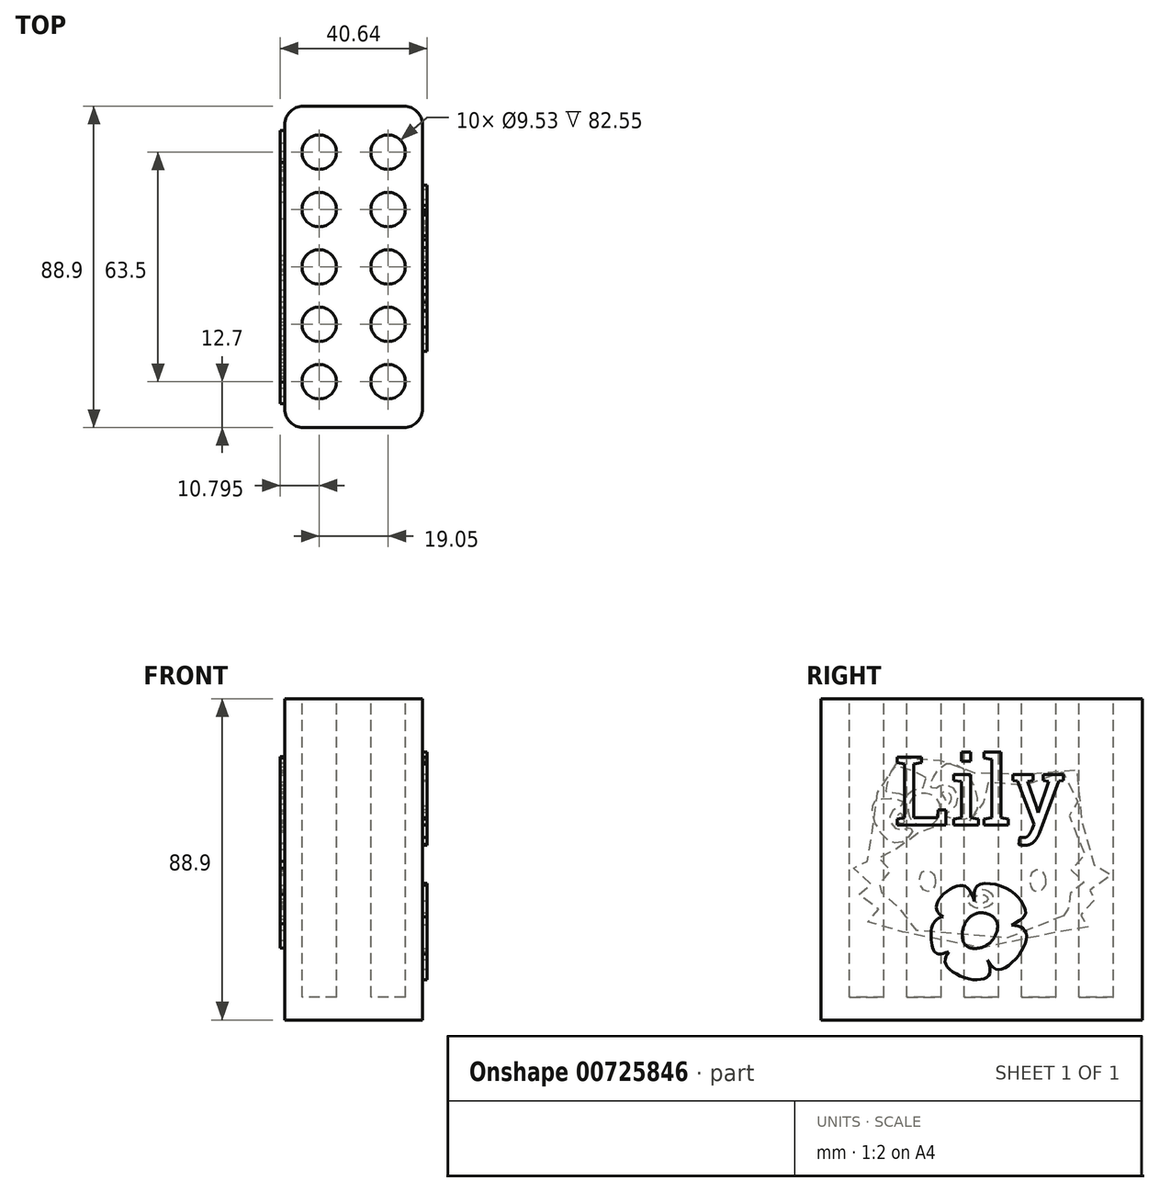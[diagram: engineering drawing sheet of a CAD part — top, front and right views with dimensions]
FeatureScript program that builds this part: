
annotation { "Feature Type Name" : "Feature", "Feature Type Description" : "" }
export const myFeature = defineFeature(function(context is Context, id is Id, definition is map)
    precondition{}
    {
        {
            var Q0;
            Q0=qCreatedBy(makeId("Right.planeOp"),FACE);
            var sketch = newSketch(context, id + "F0", { "sketchPlane" : qUnion([Q0])});
            skLineSegment(sketch, "E0.bottom", {"start": v(-44.45, 44.45) * mm, "end": v(44.45, 44.45) * mm});
            skLineSegment(sketch, "E0.top", {"start": v(-44.45, -44.45) * mm, "end": v(44.45, -44.45) * mm});
            skLineSegment(sketch, "E0.left", {"start": v(-44.45, 44.45) * mm, "end": v(-44.45, -44.45) * mm});
            skLineSegment(sketch, "E0.right", {"start": v(44.45, 44.45) * mm, "end": v(44.45, -44.45) * mm});
            skPoint(sketch, "E0.middle", {"position": v(0, 0) * mm});
            skSolve(sketch);
        }
        {
            var Q0;
            Q0=qSketchRegion(id+"F0",true);
            extrude(context, id + "F1", {"entities" : qUnion([Q0]), "endBound" : BoundingType.SYMMETRIC, "depth" : 38.1 * mm, "offsetDistance" : 25.4 * mm});
        }
        {
            var Q0;
            Q0=makeQuery(id+"F1.opExtrude","SWEPT_FACE",FACE,{"disambiguationData":[OSD([sQuery(id+"F0.wireOp",EDGE,"E0.bottom")])]});
            var sketch = newSketch(context, id + "F2", { "sketchPlane" : qUnion([Q0])});
            skCircle(sketch, "E1", {"center": v(-9.52, -31.75) * mm, "radius": 4.76 * mm});
            skCircle(sketch, "E2", {"center": v(-9.52, 0) * mm, "radius": 4.76 * mm});
            skCircle(sketch, "E3", {"center": v(-9.52, -15.88) * mm, "radius": 4.76 * mm});
            skCircle(sketch, "E4", {"center": v(-9.52, 15.88) * mm, "radius": 4.76 * mm});
            skCircle(sketch, "E5", {"center": v(-9.52, 31.75) * mm, "radius": 4.76 * mm});
            skCircle(sketch, "E6.MirrorC", {"center": v(9.52, 0) * mm, "radius": 4.76 * mm});
            skCircle(sketch, "E7.MirrorC", {"center": v(9.52, -31.75) * mm, "radius": 4.76 * mm});
            skCircle(sketch, "E8.MirrorC", {"center": v(9.52, -15.88) * mm, "radius": 4.76 * mm});
            skCircle(sketch, "E9.MirrorC", {"center": v(9.52, 15.88) * mm, "radius": 4.76 * mm});
            skCircle(sketch, "E10.MirrorC", {"center": v(9.52, 31.75) * mm, "radius": 4.76 * mm});
            skSolve(sketch);
        }
        {
            var Q0;
            Q0=qSketchRegion(id+"F2",true);
            extrude(context, id + "F3", {"entities" : qUnion([Q0]), "operationType" : NewBodyOperationType.REMOVE, "oppositeDirection" : true, "depth" : 82.55 * mm, "offsetDistance" : 25.4 * mm});
        }
        {
            var Q0;
            Q0=makeQuery(id+"F1.opExtrude","CAP_FACE",FACE,{"disambiguationData":[OSD([sQuery(id+"F0.wireOp",EDGE,"E0.bottom"),sQuery(id+"F0.wireOp",EDGE,"E0.top"),sQuery(id+"F0.wireOp",EDGE,"E0.left"),sQuery(id+"F0.wireOp",EDGE,"E0.right")])],"isStart":false});
            var sketch = newSketch(context, id + "F4", { "sketchPlane" : qUnion([Q0])});
            skText(sketch, "E11", { "text": "Lily", "fontName": "RobotoSlab-Regular.ttf"});
            const initialGuessF4  = {"E11": [-0.0243, 0.00952, 1, 0, 0.01905]};
            skSetInitialGuess(sketch, initialGuessF4);
            skSolve(sketch);
        }
        {
            var Q0;
            Q0=qSketchRegion(id+"F4",true);
            extrude(context, id + "F5", {"entities" : qUnion([Q0]), "operationType" : NewBodyOperationType.ADD, "depth" : 1.27 * mm, "offsetDistance" : 25.4 * mm});
        }
        {
            var Q0;
            Q0=makeQuery(id+"F1.opExtrude","CAP_EDGE",EDGE,{"disambiguationData":[OSD([sQuery(id+"F0.wireOp",EDGE,"E0.left")])],"isStart":false});
            var Q1;
            Q1=makeQuery(id+"F1.opExtrude","CAP_EDGE",EDGE,{"disambiguationData":[OSD([sQuery(id+"F0.wireOp",EDGE,"E0.right")])],"isStart":false});
            var Q2;
            Q2=makeQuery(id+"F1.opExtrude","CAP_EDGE",EDGE,{"disambiguationData":[OSD([sQuery(id+"F0.wireOp",EDGE,"E0.right")])],"isStart":true});
            var Q3;
            Q3=makeQuery(id+"F1.opExtrude","CAP_EDGE",EDGE,{"disambiguationData":[OSD([sQuery(id+"F0.wireOp",EDGE,"E0.left")])],"isStart":true});
            fillet(context, id + "F6", {"entities" : qUnion([Q0, Q1, Q2, Q3]), "radius" : 5.08 * mm, "tangentPropagation" : true, "allowEdgeOverflow" : false});
        }
        {
            var Q0;
            {var subQ0=sQuery(id+"F0.wireOp",EDGE,"E0.right");var subQ1=sQuery(id+"F0.wireOp",EDGE,"E0.left");var subQ2=sQuery(id+"F0.wireOp",EDGE,"E0.top");var subQ3=sQuery(id+"F0.wireOp",EDGE,"E0.bottom");Q0=makeQuery(id+"F5.boolean.opBoolean","SPLIT",FACE,{"disambiguationData":[TD([makeQuery(id+"F1.opExtrude","SWEPT_FACE",FACE,{"disambiguationData":[OSD([subQ3])]})])],"derivedFrom":makeQuery(id+"F1.opExtrude","CAP_FACE",FACE,{"disambiguationData":[OSD([subQ3,subQ2,subQ1,subQ0])],"isStart":false})});}
            var sketch = newSketch(context, id + "F7", { "sketchPlane" : qUnion([Q0])});
            skFitSpline(sketch, "E12", {"points": [v(-4.86, -18.4) * mm, v(-4.86, -23.15) * mm, v(-2.54, -24.6) * mm, v(1.63, -23.63) * mm, v(4.35, -19.56) * mm, v(3.48, -16.16) * mm, v(-1.08, -14.9) * mm, v(-4.86, -18.4) * mm]});
            skFitSpline(sketch, "E13", {"points": [v(-1.08, -14.9) * mm, v(-2.63, -9.86) * mm, v(-5.16, -7.24) * mm, v(-10.68, -9.86) * mm, v(-12.53, -13.64) * mm, v(-10.68, -15.97) * mm], "startDerivative": vector(-5.93, 23.88) * mm, "endDerivative": vector(15.22, -12.78) * mm});
            skFitSpline(sketch, "E14", {"points": [v(-4.47, -17.57) * mm, v(-10.68, -15.97) * mm, v(-13.6, -18.4) * mm, v(-13.5, -24.5) * mm, v(-11.85, -26.25) * mm, v(-4.86, -23.15) * mm], "startDerivative": vector(-29.8, 12.2) * mm, "endDerivative": vector(33.44, 19.83) * mm});
            skFitSpline(sketch, "E15", {"points": [v(-9.16, -25.52) * mm, v(-9.89, -29.04) * mm, v(-2.87, -33.2) * mm, v(2.18, -31.73) * mm, v(0, -24.4) * mm], "startDerivative": vector(-9.58, -18.07) * mm, "endDerivative": vector(-15.48, 30.39) * mm});
            skFitSpline(sketch, "E16", {"points": [v(1.63, -27.8) * mm, v(4.55, -30.51) * mm, v(10.58, -26.1) * mm, v(12.21, -20.07) * mm, v(9.2, -18.28) * mm, v(4.44, -18.85) * mm], "startDerivative": vector(13.9, -22.16) * mm, "endDerivative": vector(-25, -5.78) * mm});
            skFitSpline(sketch, "E17", {"points": [v(-2, -11.56) * mm, v(-1, -7.27) * mm, v(6.67, -7.92) * mm, v(11.4, -12.32) * mm, v(12.05, -15.34) * mm, v(8.3, -18.23) * mm], "startDerivative": vector(-1.04, 28.17) * mm, "endDerivative": vector(-25.73, -13.95) * mm});
            skSolve(sketch);
        }
        {
            var Q0;
            Q0=qSketchRegion(id+"F7",true);
            extrude(context, id + "F8", {"entities" : qUnion([Q0]), "operationType" : NewBodyOperationType.ADD, "depth" : 1.27 * mm, "offsetDistance" : 25.4 * mm});
        }
        {
            var Q0;
            Q0=makeQuery(id+"F1.opExtrude","CAP_FACE",FACE,{"disambiguationData":[OSD([sQuery(id+"F0.wireOp",EDGE,"E0.bottom"),sQuery(id+"F0.wireOp",EDGE,"E0.top"),sQuery(id+"F0.wireOp",EDGE,"E0.left"),sQuery(id+"F0.wireOp",EDGE,"E0.right")])],"isStart":true});
            var sketch = newSketch(context, id + "F9", { "sketchPlane" : qUnion([Q0])});
            skFitSpline(sketch, "E18", {"points": [v(-22.7, -15.64) * mm, v(-20.05, -17.5) * mm, v(-15, -19.89) * mm, v(-7.32, -21.74) * mm, v(3.38, -22.27) * mm, v(17.67, -19.77) * mm, v(21.35, -17.76) * mm, v(24, -15.35) * mm, v(24.27, -15) * mm, v(24.16, -14.66) * mm, v(23.37, -14.2) * mm, v(22.87, -13.33) * mm, v(23.28, -12.82) * mm, v(24.47, -12.89) * mm, v(25.28, -13.05) * mm, v(25.7, -12.94) * mm, v(26.37, -12.04) * mm, v(27.2, -10.17) * mm, v(27.48, -9.4) * mm, v(27.45, -9.11) * mm, v(27.27, -8.9) * mm, v(26.5, -8.65) * mm, v(25.8, -8.32) * mm, v(25.56, -7.73) * mm, v(25.82, -7.37) * mm, v(26.64, -7.16) * mm, v(27.64, -7.18) * mm, v(28.07, -7) * mm, v(28.36, -5.76) * mm, v(28.55, -3.62) * mm, v(28.53, -3.02) * mm, v(28.35, -2.83) * mm, v(28, -2.8) * mm, v(26.67, -2.99) * mm, v(25.65, -3.11) * mm, v(25.12, -3.14) * mm, v(24.61, -2.83) * mm, v(24.47, -2.63) * mm, v(24.51, -2.04) * mm, v(25.33, -1.48) * mm, v(26.78, -1.18) * mm, v(28.2, -0.93) * mm, v(28.46, -0.61) * mm, v(28.46, 0.39) * mm, v(28.22, 1.8) * mm, v(27.98, 2.96) * mm, v(27.52, 4.34) * mm, v(27.47, 4.39) * mm, v(27.18, 4.14) * mm, v(25.74, 3.3) * mm, v(23.42, 2.8) * mm, v(21.84, 3.07) * mm, v(20.58, 3.69) * mm, v(19.46, 4.52) * mm, v(18.5, 5.68) * mm, v(17.9, 6.57) * mm, v(17.6, 7.23) * mm, v(17.5, 7.7) * mm, v(17.4, 7.8) * mm, v(17.14, 7.72) * mm, v(15.94, 7.6) * mm, v(14.07, 7.89) * mm, v(12.84, 8.36) * mm, v(11.63, 9.25) * mm, v(10.84, 10.06) * mm, v(10.7, 10.28) * mm, v(10.6, 10.37) * mm, v(10.5, 10.3) * mm, v(10.1, 10.05) * mm, v(8.73, 9.63) * mm, v(7.2, 9.31) * mm, v(5.52, 9.16) * mm, v(3.95, 9.32) * mm, v(2.59, 9.8) * mm, v(1.24, 10.63) * mm, v(0.42, 11.8) * mm, v(0, 12.53) * mm, v(-0.49, 13.98) * mm, v(-0.58, 16.42) * mm, v(-0.26, 18.09) * mm, v(0.3, 20.32) * mm, v(0.55, 21.1) * mm, v(0.68, 21.34) * mm, v(0.58, 21.39) * mm, v(-0.33, 21.39) * mm, v(-3.85, 21.29) * mm, v(-6.48, 21.17) * mm, v(-9.03, 21.01) * mm, v(-10.65, 20.59) * mm, v(-11.67, 20.46) * mm, v(-12.7, 20.71) * mm, v(-14.98, 21.85) * mm, v(-16.95, 22.8) * mm, v(-19.76, 23.7) * mm, v(-22.15, 24.23) * mm, v(-23.69, 23.95) * mm, v(-24.9, 22.89) * mm, v(-25.83, 21.12) * mm, v(-26.45, 18.6) * mm, v(-26.58, 16.45) * mm, v(-26.37, 14.7) * mm, v(-26.03, 13.8) * mm, v(-25.87, 13.42) * mm, v(-25.73, 13.32) * mm, v(-25.35, 13.47) * mm, v(-24.67, 13.72) * mm, v(-24.13, 13.51) * mm, v(-23.91, 12.78) * mm, v(-24.38, 11.75) * mm, v(-26.02, 9.33) * mm, v(-27.42, 6.06) * mm, v(-28.21, 3.37) * mm, v(-28.6, 1.53) * mm, v(-28.84, -0.28) * mm, v(-28.87, -1.3) * mm, v(-28.8, -1.87) * mm, v(-28.48, -2.1) * mm, v(-27.35, -2.22) * mm, v(-26, -2.55) * mm, v(-25.1, -2.78) * mm, v(-24.65, -3.33) * mm, v(-24.96, -3.98) * mm, v(-26, -4.12) * mm, v(-27.34, -4.08) * mm, v(-28.23, -4.08) * mm, v(-28.5, -4.28) * mm, v(-28.53, -5) * mm, v(-28.28, -6.53) * mm, v(-27.84, -7.8) * mm, v(-27.59, -8.48) * mm, v(-27.3, -8.5) * mm, v(-26.7, -8.5) * mm, v(-25.5, -8.4) * mm, v(-24.6, -8.55) * mm, v(-24.21, -8.98) * mm, v(-24.57, -9.44) * mm, v(-25.95, -10.1) * mm, v(-26.7, -10.33) * mm, v(-26.53, -11.02) * mm, v(-25.9, -12.12) * mm, v(-25.13, -13.1) * mm, v(-24.77, -13.64) * mm, v(-24.24, -13.81) * mm, v(-23.3, -13.62) * mm, v(-21.96, -13.17) * mm, v(-21.2, -13.17) * mm, v(-20.82, -13.81) * mm, v(-21.04, -14.36) * mm, v(-22.26, -15.1) * mm, v(-22.64, -15.31) * mm, v(-22.73, -15.48) * mm, v(-22.7, -15.64) * mm]});
            skFitSpline(sketch, "E19", {"points": [v(-29.43, -18.69) * mm, v(-27.61, -17.61) * mm, v(-25.93, -16.85) * mm, v(-25.35, -16.61) * mm, v(-24.51, -17.08) * mm, v(-21.83, -19.06) * mm, v(-17.07, -21.47) * mm, v(-11.95, -23.29) * mm, v(-4.4, -24.23) * mm, v(2.24, -24.57) * mm, v(9.78, -24) * mm, v(19.8, -21.24) * mm, v(24.82, -17.78) * mm, v(26.43, -16.28) * mm, v(26.77, -15.9) * mm, v(27.23, -15.72) * mm, v(28.23, -16.02) * mm, v(30.56, -16.94) * mm, v(32.3, -17.67) * mm, v(32.87, -17.83) * mm, v(33.45, -17.38) * mm, v(33.34, -16.58) * mm, v(32.06, -15.5) * mm, v(30.15, -14.58) * mm, v(28.67, -13.95) * mm, v(28.38, -13.7) * mm, v(28.37, -13.17) * mm, v(29.21, -11.25) * mm, v(29.77, -9.94) * mm, v(30.04, -9.44) * mm, v(30.7, -9.34) * mm, v(32.26, -9.47) * mm, v(33.73, -9.7) * mm, v(35.38, -9.58) * mm, v(35.82, -9.19) * mm, v(35.4, -8.52) * mm, v(33.65, -7.86) * mm, v(31.73, -7.55) * mm, v(30.98, -7.45) * mm, v(30.65, -7.26) * mm, v(30.54, -6.95) * mm, v(30.64, -5.4) * mm, v(30.85, -3.4) * mm, v(30.85, -2.86) * mm, v(30.99, -2.63) * mm, v(31.36, -2.48) * mm, v(32.86, -2.35) * mm, v(34.6, -2.4) * mm, v(35.94, -2.42) * mm, v(36.96, -2.4) * mm, v(37.55, -2.21) * mm, v(37.8, -1.77) * mm, v(37.41, -1.23) * mm, v(35.83, -0.78) * mm, v(33.04, -0.57) * mm, v(31.39, -0.56) * mm, v(31.06, -0.48) * mm, v(30.75, 0.23) * mm, v(30.23, 3.59) * mm, v(29.5, 5.69) * mm, v(29.27, 6.34) * mm, v(29.28, 6.4) * mm, v(29.55, 6.79) * mm, v(30.72, 8.9) * mm, v(31.71, 11.95) * mm, v(31.65, 15.49) * mm, v(30.32, 17.65) * mm, v(28.79, 18.2) * mm, v(28.75, 18.27) * mm, v(28.7, 19) * mm, v(27.96, 23.26) * mm, v(26.76, 26.2) * mm, v(25.02, 27.79) * mm, v(23.03, 28.03) * mm, v(20.07, 27.57) * mm, v(15.98, 25.93) * mm, v(14.3, 24.8) * mm, v(14.18, 24.71) * mm, v(14.1, 24.76) * mm, v(11.96, 27.01) * mm, v(9.57, 28.26) * mm, v(6.5, 28.03) * mm, v(4.35, 26.75) * mm, v(2.93, 25.1) * mm, v(2.15, 24.03) * mm, v(2.06, 24) * mm, v(-0.2, 24.06) * mm, v(-5.9, 23.96) * mm, v(-10.05, 23.43) * mm, v(-11.32, 23.27) * mm, v(-13.79, 24.17) * mm, v(-19.2, 26.17) * mm, v(-22.67, 26.7) * mm, v(-25.3, 26) * mm, v(-26.87, 23.7) * mm, v(-28.56, 18.86) * mm, v(-28.71, 14.18) * mm, v(-27.71, 11.13) * mm, v(-27.75, 10.52) * mm, v(-28.2, 9.65) * mm, v(-29.48, 6.76) * mm, v(-30.81, 2.79) * mm, v(-31.1, 0) * mm, v(-31.19, -1.43) * mm, v(-31.29, -1.9) * mm, v(-31.9, -2.06) * mm, v(-35.24, -2.42) * mm, v(-37.1, -2.87) * mm, v(-37.74, -3.67) * mm, v(-37.65, -4.2) * mm, v(-35.84, -4.33) * mm, v(-33.8, -4.07) * mm, v(-32.03, -3.98) * mm, v(-31.43, -4.04) * mm, v(-31.03, -4.25) * mm, v(-30.57, -6.5) * mm, v(-30.2, -7.86) * mm, v(-30.04, -8.54) * mm, v(-30.18, -8.92) * mm, v(-30.95, -9.28) * mm, v(-32.81, -9.88) * mm, v(-34.03, -10.46) * mm, v(-34.28, -11.17) * mm, v(-33.72, -11.65) * mm, v(-32.49, -11.53) * mm, v(-30.4, -11.06) * mm, v(-29.64, -11.02) * mm, v(-28.84, -11.34) * mm, v(-28.17, -12.59) * mm, v(-27.7, -13.27) * mm, v(-27.26, -14.1) * mm, v(-27.01, -14.38) * mm, v(-26.96, -14.96) * mm, v(-27.37, -15.34) * mm, v(-29.08, -16.4) * mm, v(-30.91, -17.47) * mm, v(-31.9, -18.52) * mm, v(-31.92, -19.2) * mm, v(-31.42, -19.6) * mm, v(-30.3, -19.27) * mm, v(-29.43, -18.69) * mm]});
            skFitSpline(sketch, "E20", {"points": [v(-17.86, -6.28) * mm, v(-17.49, -4.22) * mm, v(-15.99, -2.98) * mm, v(-14.13, -3.56) * mm, v(-13.38, -5.79) * mm, v(-14, -8.1) * mm, v(-15.61, -8.84) * mm, v(-17.49, -7.65) * mm, v(-17.86, -6.28) * mm]});
            skFitSpline(sketch, "E21", {"points": [v(12.94, -5.04) * mm, v(12.94, -7.2) * mm, v(13.87, -8.62) * mm, v(15.22, -8.82) * mm, v(16.63, -7.67) * mm, v(17.07, -5.48) * mm, v(16.37, -3.47) * mm, v(14.62, -3.16) * mm, v(13.34, -4.07) * mm, v(12.94, -5.04) * mm]});
            skFitSpline(sketch, "E22", {"points": [v(-1.16, -10.05) * mm, v(-1.78, -10.98) * mm, v(-1.18, -11.76) * mm, v(0, -12.15) * mm, v(1.4, -11.93) * mm, v(2.1, -11.25) * mm, v(1.25, -9.99) * mm, v(0, -9.72) * mm, v(-1.16, -10.05) * mm]});
            skFitSpline(sketch, "E23", {"points": [v(-1.1, -8.44) * mm, v(-2.84, -9.68) * mm, v(-3.15, -11.82) * mm, v(-2.06, -13.02) * mm, v(0, -13.52) * mm, v(1.98, -13.28) * mm, v(3.55, -11.84) * mm, v(3.4, -9.92) * mm, v(1.83, -8.62) * mm, v(0.48, -8.29) * mm, v(-1.1, -8.44) * mm]});
            skFitSpline(sketch, "E24", {"points": [v(15.31, 22.6) * mm, v(17.25, 23.67) * mm, v(19.03, 24.42) * mm, v(21.52, 25.2) * mm, v(22.87, 25.56) * mm, v(23.93, 25.57) * mm, v(24.72, 24.8) * mm, v(25.46, 23.35) * mm, v(25.94, 21.79) * mm, v(26.34, 19.62) * mm, v(26.44, 18.57) * mm, v(26.32, 18.56) * mm, v(25.31, 18.54) * mm, v(22.93, 18.24) * mm, v(21.3, 17.7) * mm, v(20.97, 17.52) * mm, v(20.85, 17.39) * mm, v(20.77, 17.5) * mm, v(19.87, 18.42) * mm, v(17.87, 19.56) * mm, v(16.1, 19.88) * mm, v(16.08, 19.94) * mm, v(15.94, 20.65) * mm, v(15.47, 22.05) * mm, v(15.28, 22.5) * mm, v(15.26, 22.57) * mm, v(15.31, 22.6) * mm]});
            skFitSpline(sketch, "E25", {"points": [v(11.5, 20.28) * mm, v(12.18, 19.96) * mm, v(12.62, 19.57) * mm, v(12.89, 19.5) * mm, v(13.6, 19.76) * mm, v(14.11, 19.97) * mm, v(14.28, 20.26) * mm, v(13.72, 21.92) * mm, v(12.46, 24.1) * mm, v(10.12, 26.3) * mm, v(8.41, 26.66) * mm, v(5.77, 25.67) * mm, v(3.4, 22.88) * mm, v(1.77, 19.18) * mm, v(1.1, 14.92) * mm, v(2.1, 12.14) * mm, v(4.14, 11.04) * mm, v(7.76, 11.12) * mm, v(9.46, 11.65) * mm, v(9.66, 11.94) * mm, v(9.58, 12.46) * mm, v(9.4, 13.12) * mm, v(8.69, 13.47) * mm, v(7.5, 14.34) * mm, v(6.52, 16) * mm, v(6.8, 18.65) * mm, v(8.98, 20.41) * mm, v(10.8, 20.52) * mm, v(11.5, 20.28) * mm]});
            skFitSpline(sketch, "E26", {"points": [v(8.75, 15.67) * mm, v(8.3, 17.04) * mm, v(8.74, 18.07) * mm, v(9.5, 18.66) * mm, v(10.35, 18.67) * mm, v(10.99, 18.46) * mm, v(11.08, 18.23) * mm, v(10.87, 17.75) * mm, v(10.3, 16.97) * mm, v(9.8, 15.94) * mm, v(9.64, 15.39) * mm, v(9.43, 15.26) * mm, v(9.06, 15.38) * mm, v(8.75, 15.67) * mm]});
            skFitSpline(sketch, "E27", {"points": [v(13.33, 10.04) * mm, v(11.6, 12.3) * mm, v(11.54, 15.15) * mm, v(13.19, 17.45) * mm, v(15.83, 18.25) * mm, v(18.64, 17.39) * mm, v(20.28, 14.31) * mm, v(19.62, 11.25) * mm, v(17.56, 9.54) * mm, v(15.1, 9.33) * mm, v(13.33, 10.04) * mm]});
            skFitSpline(sketch, "E28", {"points": [v(21.53, 10.9) * mm, v(21.81, 11.6) * mm, v(22, 12.36) * mm, v(22.17, 12.57) * mm, v(22.49, 12.64) * mm, v(23.2, 12.17) * mm, v(23.5, 11.02) * mm, v(22.96, 10.26) * mm, v(22.26, 9.98) * mm, v(21.68, 10.04) * mm, v(21.37, 10.27) * mm, v(21.3, 10.47) * mm, v(21.4, 10.67) * mm, v(21.53, 10.9) * mm]});
            skFitSpline(sketch, "E29", {"points": [v(19.48, 8.54) * mm, v(19.23, 8.36) * mm, v(19.1, 8.01) * mm, v(19.7, 6.9) * mm, v(20.88, 5.51) * mm, v(22.45, 4.65) * mm, v(24.29, 4.61) * mm, v(26.42, 5.75) * mm, v(28.42, 8.16) * mm, v(30.02, 11.94) * mm, v(30.15, 14.22) * mm, v(29.96, 15.48) * mm, v(29.33, 16.2) * mm, v(28.17, 16.65) * mm, v(25.66, 16.9) * mm, v(23.55, 16.62) * mm, v(22.16, 16.27) * mm, v(21.92, 16.13) * mm, v(21.86, 15.77) * mm, v(22, 15.3) * mm, v(22.1, 14.84) * mm, v(22.26, 14.62) * mm, v(22.66, 14.51) * mm, v(24.1, 13.89) * mm, v(25.23, 12.36) * mm, v(25.37, 11.38) * mm, v(24.95, 9.7) * mm, v(23.63, 8.46) * mm, v(21.87, 8.08) * mm, v(20.46, 8.54) * mm, v(20.07, 8.8) * mm, v(19.74, 8.73) * mm, v(19.48, 8.54) * mm]});
            skSolve(sketch);
        }
        {
            var Q0;
            Q0=makeQuery(id+"F9.imprint","IMPRINT",FACE,{"disambiguationData":[TD([[makeQuery(id+"F9.imprint","IMPRINT",EDGE,{"derivedFrom":sQuery(id+"F9.wireOp",EDGE,"E18")}),-1.0]])]});
            var Q1;
            Q1=makeQuery(id+"F9.imprint","IMPRINT",FACE,{"disambiguationData":[TD([[makeQuery(id+"F9.imprint","IMPRINT",EDGE,{"derivedFrom":sQuery(id+"F9.wireOp",EDGE,"E20")}),-1.0]])]});
            var Q2;
            Q2=makeQuery(id+"F9.imprint","IMPRINT",FACE,{"disambiguationData":[TD([[makeQuery(id+"F9.imprint","IMPRINT",EDGE,{"derivedFrom":sQuery(id+"F9.wireOp",EDGE,"E22")}),-1.0]])]});
            var Q3;
            Q3=makeQuery(id+"F9.imprint","IMPRINT",FACE,{"disambiguationData":[TD([[makeQuery(id+"F9.imprint","IMPRINT",EDGE,{"derivedFrom":sQuery(id+"F9.wireOp",EDGE,"E21")}),1.0]])]});
            extrude(context, id + "F10", {"entities" : qUnion([Q0, Q1, Q2, Q3]), "operationType" : NewBodyOperationType.ADD, "depth" : 1.27 * mm, "offsetDistance" : 25.4 * mm});
        }
    });
